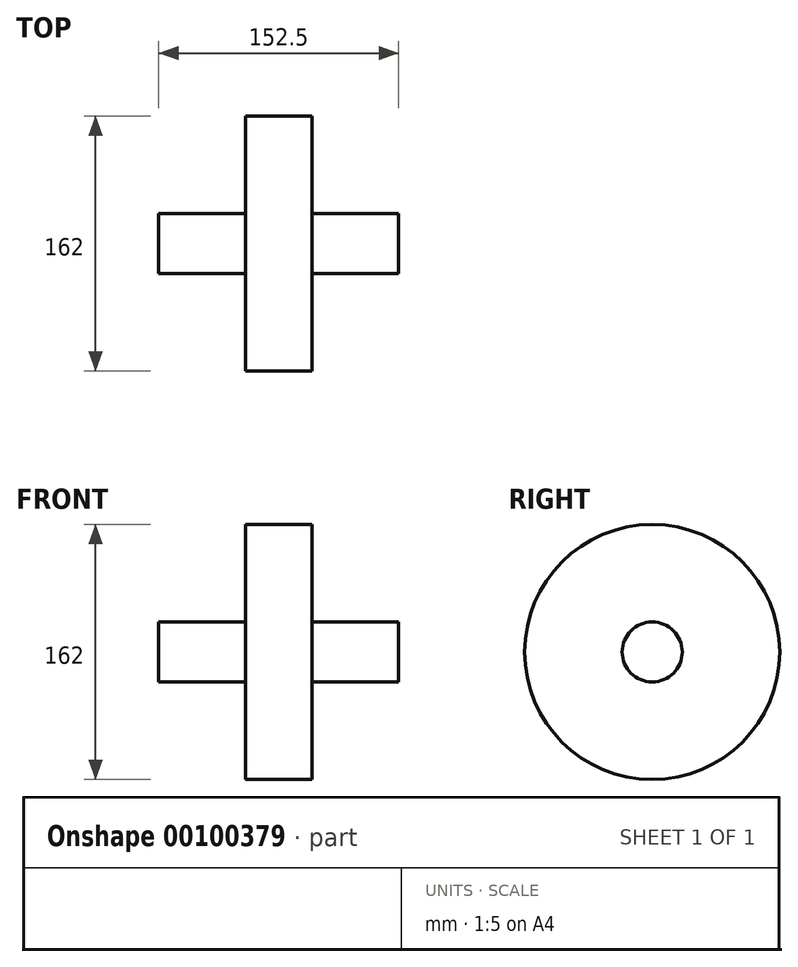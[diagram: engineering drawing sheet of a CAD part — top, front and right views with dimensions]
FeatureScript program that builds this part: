
annotation { "Feature Type Name" : "Feature", "Feature Type Description" : "" }
export const myFeature = defineFeature(function(context is Context, id is Id, definition is map)
    precondition{}
    {
        {
            var Q0;
            Q0=qCreatedBy(makeId("Right.planeOp"),FACE);
            var sketch = newSketch(context, id + "F0", { "sketchPlane" : qUnion([Q0])});
            skCircle(sketch, "E0", {"center": v(0, 0) * mm, "radius": 81 * mm});
            skSolve(sketch);
        }
        {
            var Q0;
            Q0 = qSketchRegion(id + "F0", true);
            extrude(context, id + "F1", {"entities" : qUnion([Q0]), "endBound" : BoundingType.SYMMETRIC, "depth" : 42.1 * mm});
        }
        {
            var Q0;
            Q0=qCreatedBy(makeId("Right.planeOp"),FACE);
            var sketch = newSketch(context, id + "F2", { "sketchPlane" : qUnion([Q0])});
            skCircle(sketch, "E1", {"center": v(0, 0) * mm, "radius": 19.05 * mm});
            skSolve(sketch);
        }
        {
            var Q0;
            Q0 = qSketchRegion(id + "F2", true);
            extrude(context, id + "F3", {"entities" : qUnion([Q0]), "operationType" : NewBodyOperationType.ADD, "endBound" : BoundingType.SYMMETRIC, "depth" : 152.5 * mm});
        }
        {
            var Q0;
            Q0=makeQuery(id+"F3.opExtrude","CAP_FACE",FACE,{"disambiguationData":[OSD([sQuery(id+"F2.wireOp",EDGE,"E1")])],"isStart":true});
            cPlane(context, id + "F4", {"entities" : qUnion([Q0]), "cplaneType" : CPlaneType.OFFSET, "offset" : 20 * mm, "oppositeDirection" : true, "width" : 150 * mm, "height" : 150 * mm});
        }
    });
